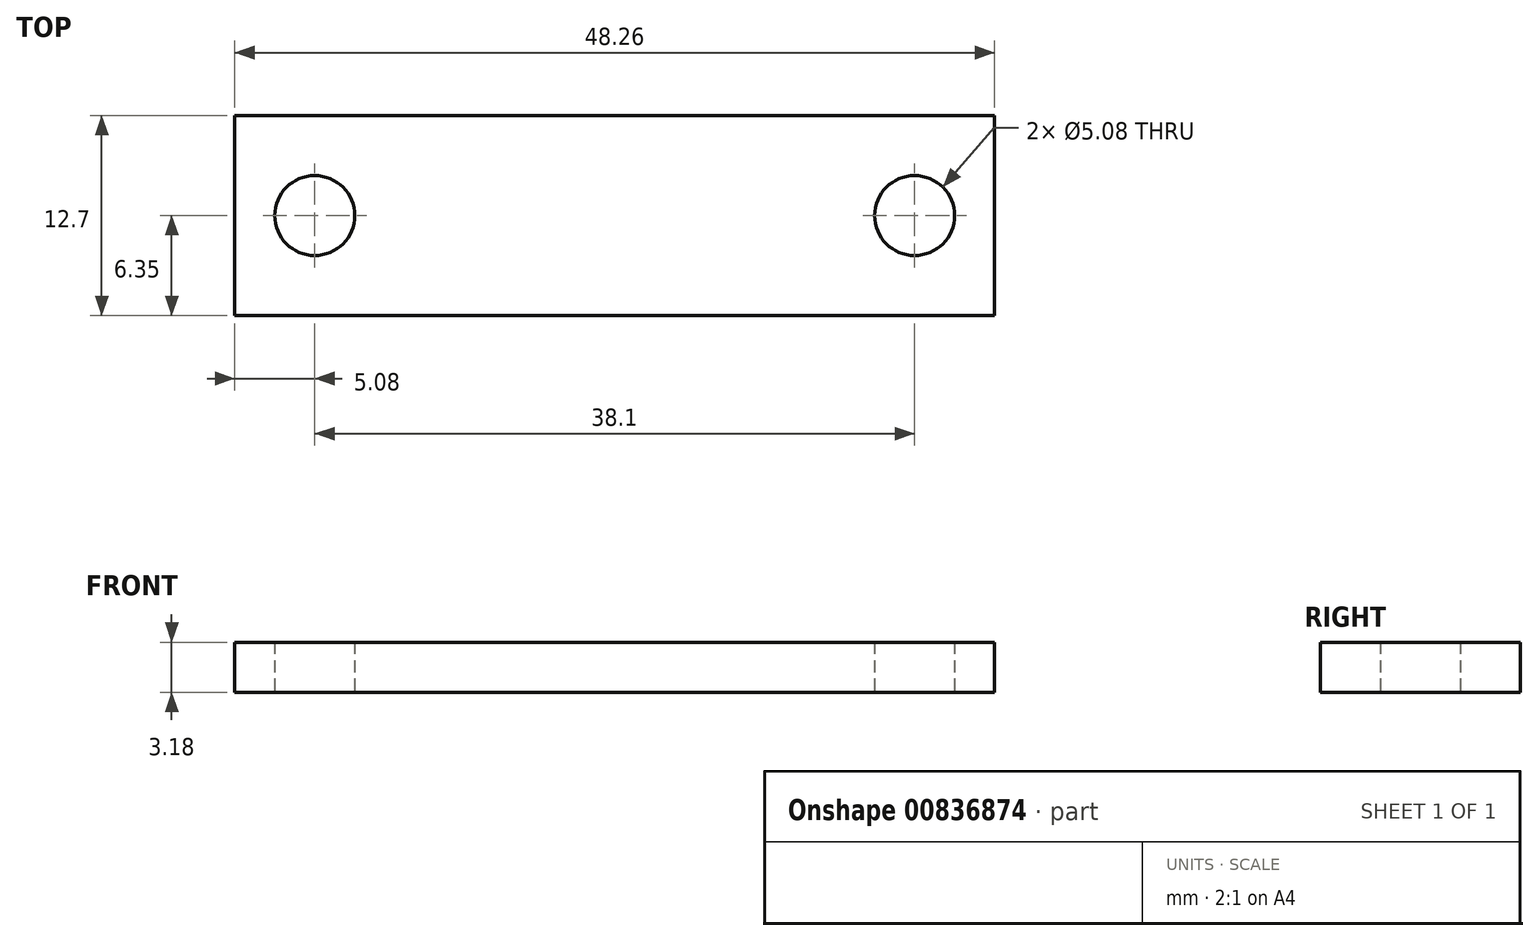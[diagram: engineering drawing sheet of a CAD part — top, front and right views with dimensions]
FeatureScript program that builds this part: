
annotation { "Feature Type Name" : "Feature", "Feature Type Description" : "" }
export const myFeature = defineFeature(function(context is Context, id is Id, definition is map)
    precondition{}
    {
        {
            var Q0;
            Q0=qCreatedBy(makeId("Top.planeOp"),FACE);
            var sketch = newSketch(context, id + "F0", { "sketchPlane" : qUnion([Q0])});
            skLineSegment(sketch, "E0.bottom", {"start": v(24.13, -6.35) * mm, "end": v(-24.13, -6.35) * mm});
            skLineSegment(sketch, "E0.top", {"start": v(24.13, 6.35) * mm, "end": v(-24.13, 6.35) * mm});
            skLineSegment(sketch, "E0.left", {"start": v(24.13, -6.35) * mm, "end": v(24.13, 6.35) * mm});
            skLineSegment(sketch, "E0.right", {"start": v(-24.13, -6.35) * mm, "end": v(-24.13, 6.35) * mm});
            skPoint(sketch, "E0.middle", {"position": v(0, 0) * mm});
            skCircle(sketch, "E1", {"center": v(-19.05, 0) * mm, "radius": 2.54 * mm});
            skCircle(sketch, "E2", {"center": v(19.05, 0) * mm, "radius": 2.54 * mm});
            skSolve(sketch);
        }
        {
            var Q0;
            Q0=makeQuery(id+"F0.imprint","IMPRINT",FACE,{"disambiguationData":[TD([[makeQuery(id+"F0.imprint","IMPRINT",EDGE,{"derivedFrom":sQuery(id+"F0.wireOp",EDGE,"E0.bottom")}),-1.0]])]});
            extrude(context, id + "F1", {"entities" : qUnion([Q0]), "depth" : 3.17 * mm, "offsetDistance" : 25.4 * mm});
        }
    });
